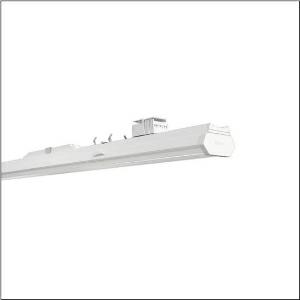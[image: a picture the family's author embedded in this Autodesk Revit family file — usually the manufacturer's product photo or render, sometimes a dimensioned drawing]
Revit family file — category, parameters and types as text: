
# Revit family: licross_r__11_protected_mo_51td11mn495g_5082
name_source: partatom
category: Lighting Fixtures
units: mm (PartAtom-declared; Revit-internal decimal feet)

## family parameters
Cut with Voids When Loaded = No
Host = Face
Light Source = No
Part Type = Normal
Room Calculation Point = No
Round Connector Dimension = Use Diameter
Shared = No

## types (1)
- --- (1 x LED, 9980 lm, 55.3 W, 4000K)
    Apparent Load = 55 VA
    CIE Flux Codes = 83 94 98 100 100
    Color Rendering = 80
    Color Temperature = 4000K
    Default Elevation = 1800 mm
    Description = Licross® 11 Protected MO, luminaire insert, of sheet steel, galvanised, coil coated, white, length: 1.500mm, width: 90mm, height: 101mm, LED rated luminous flux: 9.980lm, light colour: 840, control gear: ON/OFF Multilumen, with plug, 3-pole, with phase selection, mains connection: 220..240V, AC, 50/60Hz, rated input power: 55W, internal wiring halogen-free, primary light control with lens, of plastic, primary optical cover: cover, of PMMA, light emission: direct distribution, primary light characteristic: symmetric, protection rating (complete): IP54, insulation class (complete): insulation class I (protective earthing), certification: CE, ENEC, VDE, UKCA, protection symbol: D if used in an environment with non-conductive dust loads with corresponding accessories, impact resistance: IK06, permissible ambient temperature for indoor applications: -35..+40°C, corresponds to IFS (International Featured Standards) requirements for safety and quality in the food industry, reducing of maximum allowable ambient temperature of 5°C with ceiling mounting, LABS conformity tested according to VDMA 24364:2018-05, packaging unit: 1 piece
    Height = 92 mm
    Lamp = 1 x LED
    Lamp Light Flux = 9980 lm
    Lamp Power = 55.3 W
    Lamp count = 1
    Length = 1500 mm
    Luminous efficacy = 180 lm/W
    Manufacturer = Siteco
    ModVariant = No
    Model = 51TD11MN495G
    Mounting Place = Ceiling
    Mounting Type = Pendant
    Number of Poles = 1
    OnlyDefault = Yes
    Power Factor = 1
    Product Name = Licross® 11 Protected MO
    Product group = luminaire insert | ceiling pendant
    ProductGroupID = 902
    Protection Class = Protection class I
    Protection Degree = IP 54
    RLX_Detail_Level = 1
    RLX_Emergency_Light_Flux = 0 lm
    RLX_Emergency_Type = 0
    RLX_Emergency_Type_DB = No
    RlxData = <blob elided: 21877 chars, md5=9a4ec990>
    Socket = socket
    Standby Power = 0 W
    System Light Flux = 9980 lm
    System Power = 55 W
    Type Comments = factory setting: luminous flux: 100 % | (A | C | E) | 126 mA
    Type Image = l_1256145.jpg
    URL = http://relux.com
    VarID = @adj_107309
    Voltage = 0 V
    Weight = 0.00 kg
    Width = 88 mm

## geometry (parser evidence)
native form markers: Blend x4, Sweep x10
no freeform markers — native parametric forms only
